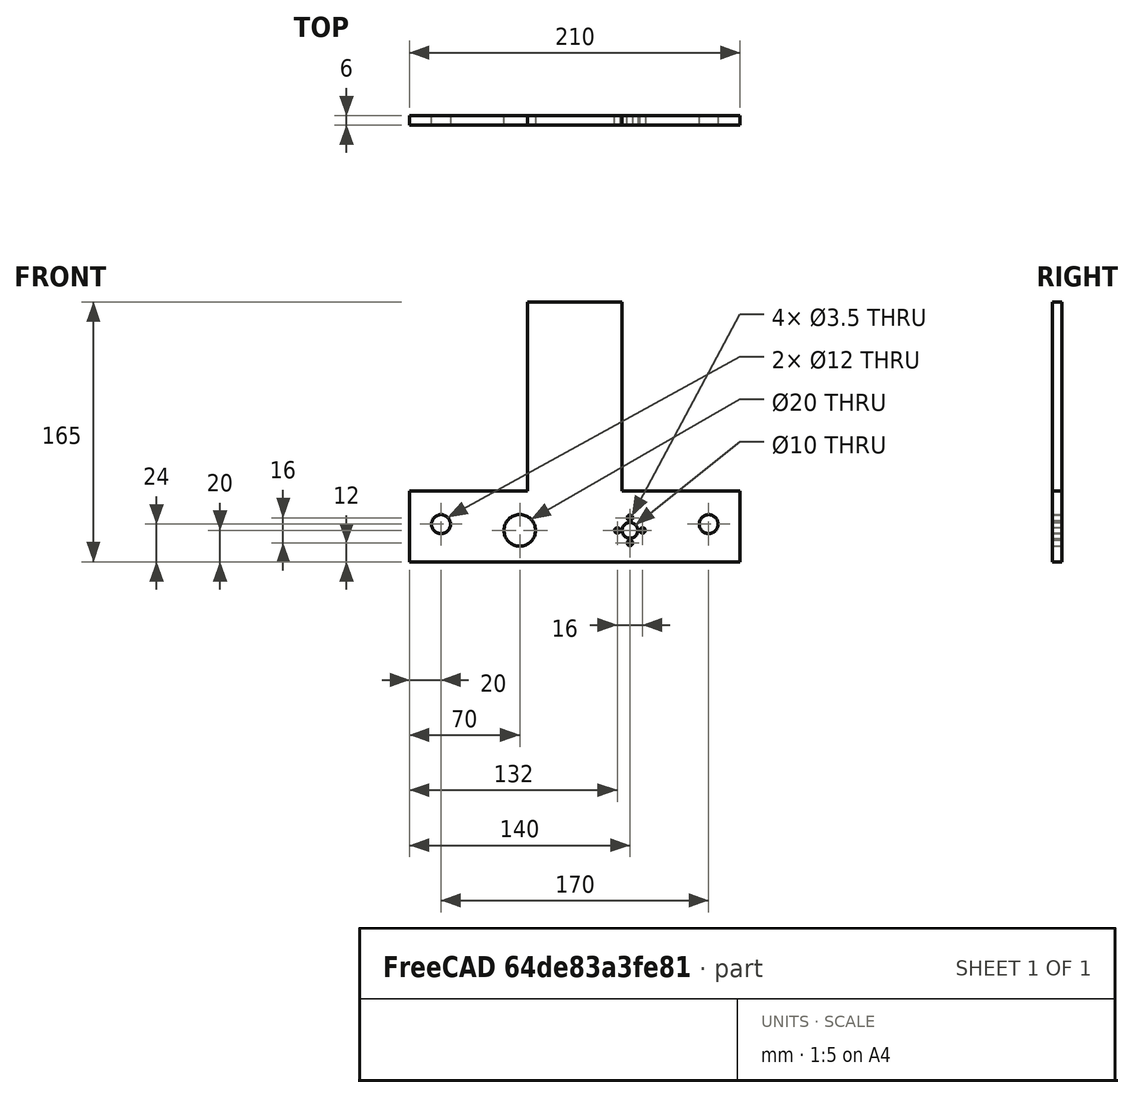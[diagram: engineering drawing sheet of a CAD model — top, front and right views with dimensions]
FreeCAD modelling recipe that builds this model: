
FCSTD DOCUMENT  (FreeCAD 0.18R4 (GitTag))
Label: pusher
License: All rights reserved
LicenseURL: http://en.wikipedia.org/wiki/All_rights_reserved
objects: Sketcher::SketchObject×1, PartDesign::Pad×1, PartDesign::Body×1
note: 4 computed .brp shape members not serialized (recipe doc carries the construction recipe); baked Part::Feature solids carry a one-line shape summary decoded from their .brp

FEATURE [Sketcher::SketchObject] Sketch
  MapMode = 5
  Placement = pos=(0,0,0) rot=(1,0,0;1.5708rad)
  Support = -> [XZ_Plane]
  sketch-geometry (16):
    g0: LineSegment StartX=0 StartY=0 StartZ=0 EndX=210 EndY=0 EndZ=0
    g1: LineSegment StartX=210 StartY=0 StartZ=0 EndX=210 EndY=45 EndZ=0
    g2: LineSegment StartX=210 StartY=45 StartZ=0 EndX=135 EndY=45 EndZ=0
    g3: LineSegment StartX=0 StartY=45 StartZ=0 EndX=0 EndY=0 EndZ=0
    g4: Circle CenterX=70 CenterY=20 CenterZ=0 NormalX=0 NormalY=0 NormalZ=1 AngleXU=0 Radius=10
    g5: Circle CenterX=140 CenterY=20 CenterZ=0 NormalX=0 NormalY=0 NormalZ=1 AngleXU=0 Radius=5
    g6: Circle CenterX=20 CenterY=24 CenterZ=0 NormalX=0 NormalY=0 NormalZ=1 AngleXU=0 Radius=6
    g7: Circle CenterX=190 CenterY=24 CenterZ=0 NormalX=0 NormalY=0 NormalZ=1 AngleXU=0 Radius=6
    g8: LineSegment StartX=135 StartY=45 StartZ=0 EndX=135 EndY=165 EndZ=0
    g9: LineSegment StartX=135 StartY=165 StartZ=0 EndX=75 EndY=165 EndZ=0
    g10: LineSegment StartX=75 StartY=165 StartZ=0 EndX=75 EndY=45 EndZ=0
    g11: LineSegment StartX=75 StartY=45 StartZ=0 EndX=0 EndY=45 EndZ=0
    g12: Circle CenterX=140 CenterY=28 CenterZ=0 NormalX=0 NormalY=0 NormalZ=1 AngleXU=0 Radius=1.75
    g13: Circle CenterX=132 CenterY=20 CenterZ=0 NormalX=0 NormalY=0 NormalZ=1 AngleXU=0 Radius=1.75
    g14: Circle CenterX=140 CenterY=12 CenterZ=0 NormalX=0 NormalY=0 NormalZ=1 AngleXU=0 Radius=1.75
    g15: Circle CenterX=148 CenterY=20 CenterZ=0 NormalX=0 NormalY=0 NormalZ=1 AngleXU=0 Radius=1.75
  constraints (46):
    c: Coincident(g0,g1)
    c: Coincident(g1,g2)
    c: Coincident(g11,g3)
    c: Coincident(g3,g0)
    c: Horizontal(g0)
    c: Horizontal(g2)
    c: Vertical(g1)
    c: Vertical(g3)
    c: Coincident(g0,g-1)
    c: DistanceX(g0,g0) = 210
    c: DistanceY(g3,g3) = 45
    c: Distance(g4,g2) = 25
    c: Radius(g4) = 10
    c: Distance(g5,g2) = 25
    c: Equal(g6,g7)
    c: Radius(g7) = 6
    c: Distance(g6,g2) = 21
    c: Distance(g6,g7) = 170
    c: Distance(g7,g2) = 21
    c: DistanceX(g6,g4) = 50
    c: DistanceX(g4,g5) = 70
    c: Distance(g7,g1) = 20
    c: Radius(g5) = 5
    c: Coincident(g8,g9)
    c: Coincident(g9,g10)
    c: Horizontal(g9)
    c: Vertical(g8)
    c: Vertical(g10)
    c: Tangent(g2,g11)
    c: Coincident(g10,g11)
    c: Coincident(g8,g2)
    c: DistanceY(g8,g8) = 120
    c: DistanceX(g9,g9) = 60
    c: DistanceX(g11,g11) = 75
    c: Equal(g13,g14)
    c: Equal(g14,g12)
    c: Equal(g12,g15)
    c: Radius(g13) = 1.75
    c: DistanceY(g5,g12) = 8
    c: DistanceY(g14,g5) = 8
    c: DistanceX(g13,g5) = 8
    c: DistanceX(g5,g14) = 0
    c: DistanceX(g12,g14) = 0
    c: DistanceX(g5,g15) = 8
    c: DistanceY(g5,g15) = 0
    c: DistanceY(g13,g15) = 0
FEATURE [PartDesign::Pad] Pad
  Length = 6
  Length2 = 100
  Placement = pos=(0,0,0) rot=(1,0,0;1.5708rad)
  Profile = -> Sketch
  Type = 0
FEATURE [PartDesign::Body] Body
  Group = -> [Sketch,Pad]
  Origin = -> Origin
  Tip = -> Pad
